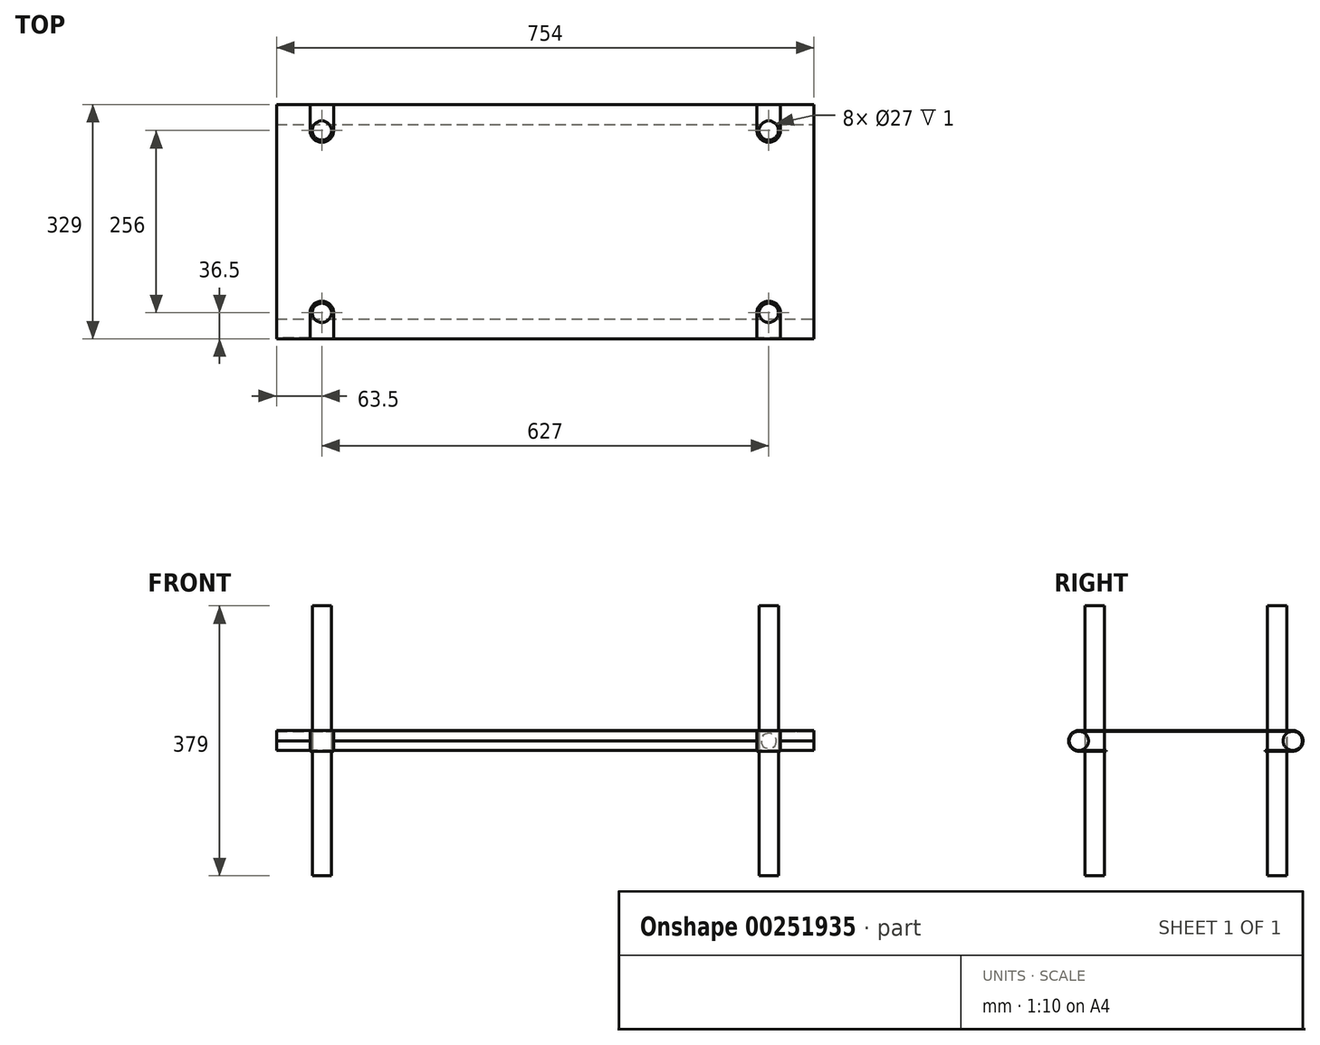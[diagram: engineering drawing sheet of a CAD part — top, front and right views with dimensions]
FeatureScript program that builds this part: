
annotation { "Feature Type Name" : "Feature", "Feature Type Description" : "" }
export const myFeature = defineFeature(function(context is Context, id is Id, definition is map)
    precondition{}
    {
        {
            var Q0;
            Q0=qCreatedBy(makeId("Right.planeOp"),FACE);
            var sketch = newSketch(context, id + "F0", { "sketchPlane" : qUnion([Q0])});
            skLineSegment(sketch, "E0", {"start": v(0, 0) * mm, "end": v(-150, 0) * mm});
            skArc(sketch, "E1", {"start": v(-150, 0) * mm, "mid": v(-160.25, -4.25) * mm, "end": v(-164.5, -14.5) * mm});
            skLineSegment(sketch, "E2", {"start": v(-164.5, -14.5) * mm, "end": v(-167.15, -14.5) * mm, "construction": true});
            skArc(sketch, "E3.0", {"start": v(-150, -1) * mm, "mid": v(-159.55, -4.95) * mm, "end": v(-163.5, -14.5) * mm});
            skLineSegment(sketch, "E3.1", {"start": v(0, -1) * mm, "end": v(-150, -1) * mm});
            skLineSegment(sketch, "E4", {"start": v(-164.5, -14.5) * mm, "end": v(-163.5, -14.5) * mm});
            skLineSegment(sketch, "E5", {"start": v(0, 0) * mm, "end": v(0, -1) * mm});
            skSolve(sketch);
        }
        {
            var Q0;
            Q0 = qSketchRegion(id + "F0", true);
            extrude(context, id + "F1", {"entities" : qUnion([Q0]), "oppositeDirection" : true, "depth" : 377 * mm});
        }
        {
            var Q0;
            Q0=makeQuery(id+"F1.opExtrude","SWEPT_FACE",FACE,{"disambiguationData":[OSD([sQuery(id+"F0.wireOp",EDGE,"E0")])]});
            var sketch = newSketch(context, id + "F2", { "sketchPlane" : qUnion([Q0])});
            skCircle(sketch, "E6", {"center": v(-63.5, -150) * mm, "radius": 13.5 * mm, "construction": true});
            skCircle(sketch, "E7", {"center": v(-63.5, -128) * mm, "radius": 13.5 * mm, "construction": true});
            skLineSegment(sketch, "E8", {"start": v(-63.5, -136.5) * mm, "end": v(-63.5, -141.5) * mm, "construction": true});
            skCircle(sketch, "E9", {"center": v(-63.5, -128) * mm, "radius": 16.5 * mm});
            skLineSegment(sketch, "E10", {"start": v(-80, -128) * mm, "end": v(-80, -173) * mm});
            skLineSegment(sketch, "E11", {"start": v(-80, -173) * mm, "end": v(-47, -173) * mm});
            skLineSegment(sketch, "E12", {"start": v(-47, -128) * mm, "end": v(-47, -173) * mm});
            skSolve(sketch);
        }
        {
            var Q0;
            Q0 = qSketchRegion(id + "F2", true);
            extrude(context, id + "F3", {"entities" : qUnion([Q0]), "operationType" : NewBodyOperationType.REMOVE, "oppositeDirection" : true, "depth" : 25 * mm});
        }
        {
            var Q0;
            Q0=makeQuery(id+"F1.opExtrude","SWEPT_BODY",BODY,{"disambiguationData":[OSD([sQuery(id+"F0.wireOp",EDGE,"E0"),sQuery(id+"F0.wireOp",EDGE,"E1"),sQuery(id+"F0.wireOp",EDGE,"E3.0"),sQuery(id+"F0.wireOp",EDGE,"E3.1"),sQuery(id+"F0.wireOp",EDGE,"E4"),sQuery(id+"F0.wireOp",EDGE,"E5")])]});
            var Q1;
            Q1=qCreatedBy(makeId("Front.planeOp"),FACE);
            mirror(context, id + "F4", {"operationType" : NewBodyOperationType.ADD, "entities" : qUnion([Q0]), "mirrorPlane" : qUnion([Q1])});
        }
        {
            var Q0;
            Q0=makeQuery(id+"F1.opExtrude","SWEPT_BODY",BODY,{"disambiguationData":[OSD([sQuery(id+"F0.wireOp",EDGE,"E0"),sQuery(id+"F0.wireOp",EDGE,"E1"),sQuery(id+"F0.wireOp",EDGE,"E3.0"),sQuery(id+"F0.wireOp",EDGE,"E3.1"),sQuery(id+"F0.wireOp",EDGE,"E4"),sQuery(id+"F0.wireOp",EDGE,"E5")])]});
            var Q1;
            {var subQ0=makeQuery(id+"F1.opExtrude","CAP_FACE",FACE,{"disambiguationData":[OSD([sQuery(id+"F0.wireOp",EDGE,"E0"),sQuery(id+"F0.wireOp",EDGE,"E1"),sQuery(id+"F0.wireOp",EDGE,"E3.0"),sQuery(id+"F0.wireOp",EDGE,"E3.1"),sQuery(id+"F0.wireOp",EDGE,"E4"),sQuery(id+"F0.wireOp",EDGE,"E5")])],"isStart":false});Q1=makeQuery(id+"F4.boolean.opBoolean","MERGE",FACE,{"derivedFrom":[subQ0,makeQuery(id+"F4.opPattern","COPY",FACE,{"derivedFrom":subQ0,"instanceName":"1"})]});}
            mirror(context, id + "F5", {"operationType" : NewBodyOperationType.ADD, "entities" : qUnion([Q0]), "mirrorPlane" : qUnion([Q1])});
        }
        {
            var Q0;
            {var subQ0=makeQuery(id+"F1.opExtrude","CAP_FACE",FACE,{"disambiguationData":[OSD([sQuery(id+"F0.wireOp",EDGE,"E0"),sQuery(id+"F0.wireOp",EDGE,"E1"),sQuery(id+"F0.wireOp",EDGE,"E3.0"),sQuery(id+"F0.wireOp",EDGE,"E3.1"),sQuery(id+"F0.wireOp",EDGE,"E4"),sQuery(id+"F0.wireOp",EDGE,"E5")])],"isStart":true});Q0=makeQuery(id+"F4.boolean.opBoolean","MERGE",FACE,{"derivedFrom":[subQ0,makeQuery(id+"F4.opPattern","COPY",FACE,{"derivedFrom":subQ0,"instanceName":"1"})]});}
            var sketch = newSketch(context, id + "F6", { "sketchPlane" : qUnion([Q0])});
            skCircle(sketch, "E13", {"center": v(-150, -14.5) * mm, "radius": 13.5 * mm});
            skSolve(sketch);
        }
        {
            var Q0;
            Q0 = qSketchRegion(id + "F6", true);
            extrude(context, id + "F7", {"entities" : qUnion([Q0]), "oppositeDirection" : true, "depth" : 754 * mm});
        }
        {
            var Q0;
            Q0=makeQuery(id+"F7.opExtrude","SWEPT_BODY",BODY,{"disambiguationData":[OSD([sQuery(id+"F6.wireOp",EDGE,"E13")])]});
            var Q1;
            Q1=qCreatedBy(makeId("Front.planeOp"),FACE);
            mirror(context, id + "F8", {"entities" : qUnion([Q0]), "mirrorPlane" : qUnion([Q1])});
        }
        {
            var Q0;
            {var subQ0=makeQuery(id+"F1.opExtrude","SWEPT_FACE",FACE,{"disambiguationData":[OSD([sQuery(id+"F0.wireOp",EDGE,"E0")])]});var subQ1=makeQuery(id+"F4.boolean.opBoolean","MERGE",FACE,{"derivedFrom":[subQ0,makeQuery(id+"F4.opPattern","COPY",FACE,{"derivedFrom":subQ0,"instanceName":"1"})]});Q0=makeQuery(id+"F5.boolean.opBoolean","MERGE",FACE,{"derivedFrom":[subQ1,makeQuery(id+"F5.opPattern","COPY",FACE,{"derivedFrom":subQ1,"instanceName":"1"})]});}
            var sketch = newSketch(context, id + "F9", { "sketchPlane" : qUnion([Q0])});
            skArc(sketch, "E14.0", {"start": v(-47, 128) * mm, "mid": v(-63.5, 111.5) * mm, "end": v(-80, 128) * mm});
            skLineSegment(sketch, "E14.1", {"start": v(-80, 128) * mm, "end": v(-80, 150) * mm});
            skLineSegment(sketch, "E14.2", {"start": v(-80, 150) * mm, "end": v(-80, 164.5) * mm});
            skLineSegment(sketch, "E14.3", {"start": v(-47, 128) * mm, "end": v(-47, 150) * mm});
            skLineSegment(sketch, "E14.4", {"start": v(-47, 150) * mm, "end": v(-47, 164.5) * mm});
            skLineSegment(sketch, "E15", {"start": v(-80, 164.5) * mm, "end": v(-47, 164.5) * mm});
            skSolve(sketch);
        }
        {
            var Q0;
            Q0 = qSketchRegion(id + "F9", true);
            extrude(context, id + "F10", {"entities" : qUnion([Q0]), "oppositeDirection" : true, "depth" : 29 * mm});
        }
        {
            var Q0;
            Q0=makeQuery(id+"F10.opExtrude","CAP_EDGE",EDGE,{"disambiguationData":[OSD([sQuery(id+"F9.wireOp",EDGE,"E15")])],"isStart":true});
            var Q1;
            Q1=makeQuery(id+"F10.opExtrude","CAP_EDGE",EDGE,{"disambiguationData":[OSD([sQuery(id+"F9.wireOp",EDGE,"E15")])],"isStart":false});
            fillet(context, id + "F11", {"entities" : qUnion([Q0, Q1]), "radius" : 14.5 * mm, "tangentPropagation" : true, "allowEdgeOverflow" : false});
        }
        {
            var Q0;
            Q0=makeQuery(id+"F10.opExtrude","SWEPT_FACE",FACE,{"disambiguationData":[OSD([sQuery(id+"F9.wireOp",EDGE,"E14.3"),sQuery(id+"F9.wireOp",EDGE,"E14.4")])]});
            var Q1;
            Q1=makeQuery(id+"F10.opExtrude","SWEPT_FACE",FACE,{"disambiguationData":[OSD([sQuery(id+"F9.wireOp",EDGE,"E14.0")])]});
            var Q2;
            Q2=makeQuery(id+"F10.opExtrude","SWEPT_FACE",FACE,{"disambiguationData":[OSD([sQuery(id+"F9.wireOp",EDGE,"E14.1"),sQuery(id+"F9.wireOp",EDGE,"E14.2")])]});
            shell(context, id + "F12", {"entities" : qUnion([Q0, Q1, Q2]), "thickness" : 1 * mm});
        }
        {
            var Q0;
            Q0=makeQuery(id+"F10.opExtrude","CAP_FACE",FACE,{"disambiguationData":[OSD([sQuery(id+"F9.wireOp",EDGE,"E14.0"),sQuery(id+"F9.wireOp",EDGE,"E14.1"),sQuery(id+"F9.wireOp",EDGE,"E14.2"),sQuery(id+"F9.wireOp",EDGE,"E14.3"),sQuery(id+"F9.wireOp",EDGE,"E14.4"),sQuery(id+"F9.wireOp",EDGE,"E15")])],"isStart":true});
            var sketch = newSketch(context, id + "F13", { "sketchPlane" : qUnion([Q0])});
            skCircle(sketch, "E16", {"center": v(-63.5, 128) * mm, "radius": 13.5 * mm});
            skSolve(sketch);
        }
        {
            var Q0;
            Q0 = qSketchRegion(id + "F13", true);
            extrude(context, id + "F14", {"entities" : qUnion([Q0]), "operationType" : NewBodyOperationType.REMOVE, "oppositeDirection" : true, "depth" : 29 * mm});
        }
        {
            var Q0;
            {var subQ0=makeQuery(id+"F1.opExtrude","CAP_FACE",FACE,{"disambiguationData":[OSD([sQuery(id+"F0.wireOp",EDGE,"E0"),sQuery(id+"F0.wireOp",EDGE,"E1"),sQuery(id+"F0.wireOp",EDGE,"E3.0"),sQuery(id+"F0.wireOp",EDGE,"E3.1"),sQuery(id+"F0.wireOp",EDGE,"E4"),sQuery(id+"F0.wireOp",EDGE,"E5")])],"isStart":true});Q0=makeQuery(id+"F4.boolean.opBoolean","MERGE",FACE,{"derivedFrom":[subQ0,makeQuery(id+"F4.opPattern","COPY",FACE,{"derivedFrom":subQ0,"instanceName":"1"})]});}
            cPlane(context, id + "F15", {"entities" : qUnion([Q0]), "cplaneType" : CPlaneType.OFFSET, "offset" : 377 * mm, "oppositeDirection" : true, "width" : 150 * mm, "height" : 150 * mm});
        }
        {
            var Q0;
            Q0=makeQuery(id+"F10.opExtrude","SWEPT_BODY",BODY,{"disambiguationData":[OSD([sQuery(id+"F9.wireOp",EDGE,"E14.0"),sQuery(id+"F9.wireOp",EDGE,"E14.1"),sQuery(id+"F9.wireOp",EDGE,"E14.2"),sQuery(id+"F9.wireOp",EDGE,"E14.3"),sQuery(id+"F9.wireOp",EDGE,"E14.4"),sQuery(id+"F9.wireOp",EDGE,"E15")])]});
            var Q1;
            Q1=qCreatedBy(id+"F15.planeOp",FACE);
            mirror(context, id + "F16", {"entities" : qUnion([Q0]), "mirrorPlane" : qUnion([Q1])});
        }
        {
            var Q0;
            Q0=makeQuery(id+"F16.opPattern","COPY",BODY,{"derivedFrom":makeQuery(id+"F10.opExtrude","SWEPT_BODY",BODY,{"disambiguationData":[OSD([sQuery(id+"F9.wireOp",EDGE,"E14.0"),sQuery(id+"F9.wireOp",EDGE,"E14.1"),sQuery(id+"F9.wireOp",EDGE,"E14.2"),sQuery(id+"F9.wireOp",EDGE,"E14.3"),sQuery(id+"F9.wireOp",EDGE,"E14.4"),sQuery(id+"F9.wireOp",EDGE,"E15")])]}),"instanceName":"1"});
            var Q1;
            Q1=makeQuery(id+"F10.opExtrude","SWEPT_BODY",BODY,{"disambiguationData":[OSD([sQuery(id+"F9.wireOp",EDGE,"E14.0"),sQuery(id+"F9.wireOp",EDGE,"E14.1"),sQuery(id+"F9.wireOp",EDGE,"E14.2"),sQuery(id+"F9.wireOp",EDGE,"E14.3"),sQuery(id+"F9.wireOp",EDGE,"E14.4"),sQuery(id+"F9.wireOp",EDGE,"E15")])]});
            var Q2;
            Q2=qCreatedBy(makeId("Front.planeOp"),FACE);
            mirror(context, id + "F17", {"entities" : qUnion([Q0, Q1]), "mirrorPlane" : qUnion([Q2])});
        }
        {
            var Q0;
            {var subQ0=makeQuery(id+"F1.opExtrude","SWEPT_FACE",FACE,{"disambiguationData":[OSD([sQuery(id+"F0.wireOp",EDGE,"E0")])]});var subQ1=makeQuery(id+"F4.boolean.opBoolean","MERGE",FACE,{"derivedFrom":[subQ0,makeQuery(id+"F4.opPattern","COPY",FACE,{"derivedFrom":subQ0,"instanceName":"1"})]});Q0=makeQuery(id+"F5.boolean.opBoolean","MERGE",FACE,{"derivedFrom":[subQ1,makeQuery(id+"F5.opPattern","COPY",FACE,{"derivedFrom":subQ1,"instanceName":"1"})]});}
            var sketch = newSketch(context, id + "F18", { "sketchPlane" : qUnion([Q0])});
            skCircle(sketch, "E17.0", {"center": v(-690.5, 128) * mm, "radius": 13.5 * mm});
            skCircle(sketch, "E17.1", {"center": v(-690.5, -128) * mm, "radius": 13.5 * mm});
            skCircle(sketch, "E17.2", {"center": v(-63.5, 128) * mm, "radius": 13.5 * mm});
            skCircle(sketch, "E17.3", {"center": v(-63.5, -128) * mm, "radius": 13.5 * mm});
            skSolve(sketch);
        }
        {
            var Q0;
            Q0 = qSketchRegion(id + "F18", true);
            extrude(context, id + "F19", {"entities" : qUnion([Q0]), "depth" : 175 * mm, "hasSecondDirection" : true, "secondDirectionOppositeDirection" : true, "secondDirectionDepth" : 204 * mm});
        }
    });
